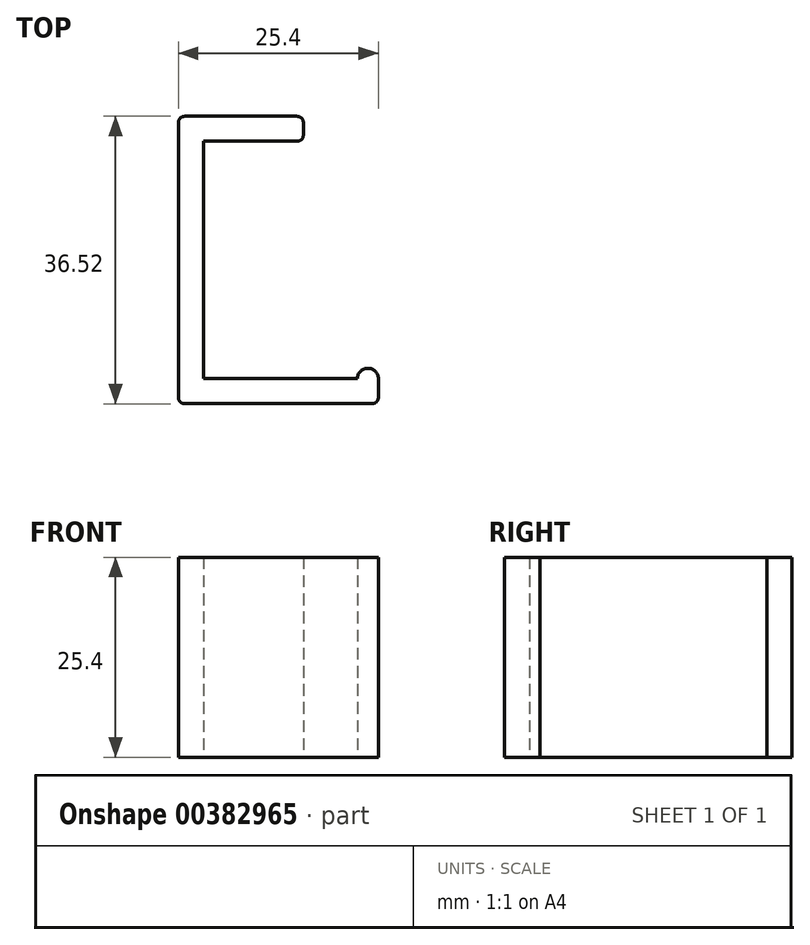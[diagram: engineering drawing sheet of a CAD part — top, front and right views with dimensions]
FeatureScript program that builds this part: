
annotation { "Feature Type Name" : "Feature", "Feature Type Description" : "" }
export const myFeature = defineFeature(function(context is Context, id is Id, definition is map)
    precondition{}
    {
        {
            var Q0;
            Q0=qCreatedBy(makeId("Top.planeOp"),FACE);
            var sketch = newSketch(context, id + "F0", { "sketchPlane" : qUnion([Q0])});
            skLineSegment(sketch, "E0", {"start": v(-22.23, 0) * mm, "end": v(-22.23, 30.16) * mm});
            skLineSegment(sketch, "E1", {"start": v(-22.23, 30.16) * mm, "end": v(-10.32, 30.16) * mm});
            skLineSegment(sketch, "E2.0", {"start": v(-24.6, 33.34) * mm, "end": v(-10.32, 33.34) * mm});
            skLineSegment(sketch, "E2.1", {"start": v(-25.4, -2.38) * mm, "end": v(-25.4, 32.54) * mm});
            skLineSegment(sketch, "E2.2", {"start": v(-0.8, -3.18) * mm, "end": v(-24.6, -3.18) * mm});
            skLineSegment(sketch, "E3", {"start": v(-9.52, 32.54) * mm, "end": v(-9.52, 30.96) * mm});
            skLineSegment(sketch, "E4", {"start": v(0, 0) * mm, "end": v(0, -2.38) * mm});
            skLineSegment(sketch, "E5", {"start": v(-2.66, 0) * mm, "end": v(-22.23, 0) * mm});
            skArc(sketch, "E6", {"start": v(0, 0) * mm, "mid": v(-1.33, 1.33) * mm, "end": v(-2.66, 0) * mm});
            skPoint(sketch, "E7.visualSharp", {"position": v(0, -3.18) * mm});
            skArc(sketch, "E7.filletArc", {"start": v(-0.8, -3.18) * mm, "mid": v(-0.23, -2.94) * mm, "end": v(0, -2.38) * mm});
            skPoint(sketch, "E8.visualSharp", {"position": v(-25.4, -3.18) * mm});
            skArc(sketch, "E8.filletArc", {"start": v(-25.4, -2.38) * mm, "mid": v(-25.17, -2.94) * mm, "end": v(-24.6, -3.18) * mm});
            skPoint(sketch, "E9.visualSharp", {"position": v(-25.4, 33.34) * mm});
            skArc(sketch, "E9.filletArc", {"start": v(-24.6, 33.34) * mm, "mid": v(-25.17, 33.1) * mm, "end": v(-25.4, 32.54) * mm});
            skPoint(sketch, "E10.visualSharp", {"position": v(-9.52, 33.34) * mm});
            skArc(sketch, "E10.filletArc", {"start": v(-9.52, 32.54) * mm, "mid": v(-9.76, 33.1) * mm, "end": v(-10.32, 33.34) * mm});
            skPoint(sketch, "E11.visualSharp", {"position": v(-9.52, 30.16) * mm});
            skArc(sketch, "E11.filletArc", {"start": v(-10.32, 30.16) * mm, "mid": v(-9.76, 30.4) * mm, "end": v(-9.53, 30.96) * mm});
            skSolve(sketch);
        }
        {
            var Q0;
            Q0=makeQuery(id+"F0.imprint","IMPRINT",FACE,{"disambiguationData":[TD([[makeQuery(id+"F0.imprint","IMPRINT",EDGE,{"derivedFrom":sQuery(id+"F0.wireOp",EDGE,"E0")}),1.0]])]});
            extrude(context, id + "F1", {"entities" : qUnion([Q0]), "depth" : 25.4 * mm});
        }
    });
